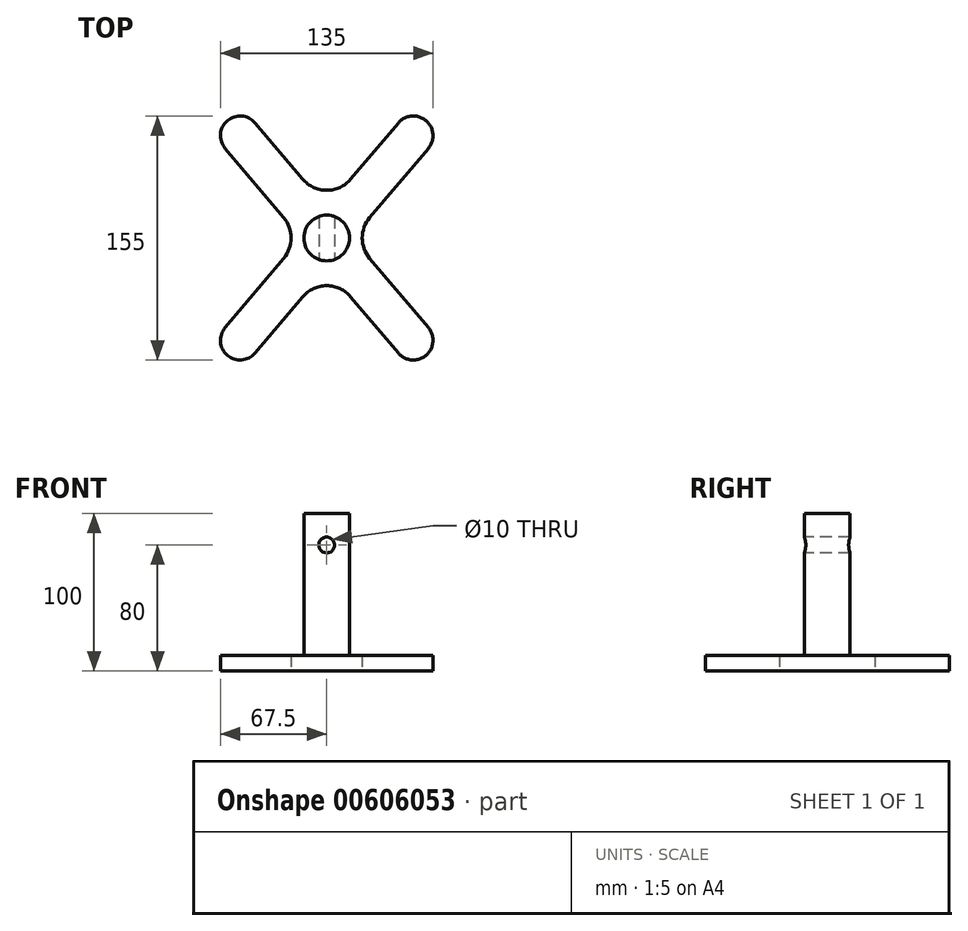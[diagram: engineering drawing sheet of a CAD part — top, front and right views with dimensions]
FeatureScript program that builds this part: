
annotation { "Feature Type Name" : "Feature", "Feature Type Description" : "" }
export const myFeature = defineFeature(function(context is Context, id is Id, definition is map)
    precondition{}
    {
        {
            var Q0;
            Q0=qCreatedBy(makeId("Top.planeOp"),FACE);
            var sketch = newSketch(context, id + "F0", { "sketchPlane" : qUnion([Q0])});
            skPoint(sketch, "E0.middle", {"position": v(0, 0) * mm});
            skLineSegment(sketch, "E1", {"start": v(-55, 65) * mm, "end": v(55, -65) * mm});
            skLineSegment(sketch, "E2", {"start": v(-55, -65) * mm, "end": v(55, 65) * mm});
            skCircle(sketch, "E3", {"center": v(-55, -65) * mm, "radius": 12.5 * mm});
            skCircle(sketch, "E4", {"center": v(-55, 65) * mm, "radius": 12.5 * mm});
            skCircle(sketch, "E5", {"center": v(55, 65) * mm, "radius": 12.5 * mm});
            skCircle(sketch, "E6", {"center": v(55, -65) * mm, "radius": 12.5 * mm});
            skLineSegment(sketch, "E7", {"start": v(-55, -65) * mm, "end": v(-64.54, -56.93) * mm});
            skLineSegment(sketch, "E8", {"start": v(-64.54, -56.93) * mm, "end": v(-45.46, -73.07) * mm});
            skLineSegment(sketch, "E9", {"start": v(-55, 65) * mm, "end": v(-64.54, 56.93) * mm});
            skLineSegment(sketch, "E10", {"start": v(-64.54, 56.93) * mm, "end": v(-45.46, 73.07) * mm});
            skLineSegment(sketch, "E11", {"start": v(55, 65) * mm, "end": v(45.46, 73.07) * mm});
            skLineSegment(sketch, "E12", {"start": v(45.46, 73.07) * mm, "end": v(64.54, 56.93) * mm});
            skLineSegment(sketch, "E13", {"start": v(55, -65) * mm, "end": v(45.46, -73.07) * mm});
            skLineSegment(sketch, "E14", {"start": v(45.46, -73.07) * mm, "end": v(64.54, -56.93) * mm});
            skLineSegment(sketch, "E15", {"start": v(-45.46, -73.07) * mm, "end": v(-15.27, -37.4) * mm});
            skLineSegment(sketch, "E16", {"start": v(-64.54, -56.93) * mm, "end": v(-27.3, -12.92) * mm});
            skLineSegment(sketch, "E17", {"start": v(-64.54, 56.93) * mm, "end": v(-27.3, 12.92) * mm});
            skLineSegment(sketch, "E18", {"start": v(64.54, -56.93) * mm, "end": v(27.3, -12.92) * mm});
            skArc(sketch, "E19.filletArc", {"start": v(-27.3, -12.92) * mm, "mid": v(-22.57, 0) * mm, "end": v(-27.3, 12.92) * mm});
            skLineSegment(sketch, "E20", {"start": v(45.46, -73.07) * mm, "end": v(15.27, -37.4) * mm});
            skArc(sketch, "E21.filletArc", {"start": v(15.27, -37.4) * mm, "mid": v(0, -30.31) * mm, "end": v(-15.27, -37.4) * mm});
            skLineSegment(sketch, "E22", {"start": v(45.46, 73.07) * mm, "end": v(15.27, 37.4) * mm});
            skLineSegment(sketch, "E23", {"start": v(64.54, 56.93) * mm, "end": v(27.3, 12.92) * mm});
            skArc(sketch, "E24.filletArc", {"start": v(27.3, 12.92) * mm, "mid": v(22.57, 0) * mm, "end": v(27.3, -12.92) * mm});
            skLineSegment(sketch, "E25", {"start": v(-45.46, 73.07) * mm, "end": v(-15.27, 37.4) * mm});
            skArc(sketch, "E26.filletArc", {"start": v(-15.27, 37.4) * mm, "mid": v(0, 30.31) * mm, "end": v(15.27, 37.4) * mm});
            skCircle(sketch, "E27", {"center": v(0, 0) * mm, "radius": 14.5 * mm});
            skSolve(sketch);
        }
        {
            var Q0;
            {var subQ0=sQuery(id+"F0.wireOp",EDGE,"E10");var subQ4=makeQuery(id+"F0.imprint","INTERSECT",VERTEX,{"derivedFrom":[sQuery(id+"F0.wireOp",EDGE,"E1"),subQ0]});Q0=makeQuery(id+"F0.imprint","IMPRINT",FACE,{"disambiguationData":[TD([[makeQuery(id+"F0.imprint","IMPRINT",EDGE,{"disambiguationData":[TD([[subQ4,1.0]])],"derivedFrom":subQ0}),1.0]])]});}
            var Q1;
            {var subQ0=sQuery(id+"F0.wireOp",EDGE,"E10");var subQ1=sQuery(id+"F0.wireOp",EDGE,"E1");var subQ2=makeQuery(id+"F0.imprint","INTERSECT",VERTEX,{"derivedFrom":[subQ1,subQ0]});Q1=makeQuery(id+"F0.imprint","IMPRINT",FACE,{"disambiguationData":[TD([[makeQuery(id+"F0.imprint","IMPRINT",EDGE,{"disambiguationData":[TD([[subQ2,-1.0]])],"derivedFrom":subQ1}),1.0]])]});}
            var Q2;
            {var subQ0=sQuery(id+"F0.wireOp",EDGE,"E10");var subQ1=sQuery(id+"F0.wireOp",EDGE,"E1");var subQ2=makeQuery(id+"F0.imprint","INTERSECT",VERTEX,{"derivedFrom":[subQ1,subQ0]});Q2=makeQuery(id+"F0.imprint","IMPRINT",FACE,{"disambiguationData":[TD([[makeQuery(id+"F0.imprint","IMPRINT",EDGE,{"disambiguationData":[TD([[subQ2,-1.0]])],"derivedFrom":subQ1}),-1.0]])]});}
            var Q3;
            {var subQ0=sQuery(id+"F0.wireOp",EDGE,"E22");Q3=makeQuery(id+"F0.imprint","IMPRINT",FACE,{"disambiguationData":[TD([[makeQuery(id+"F0.imprint","IMPRINT",EDGE,{"derivedFrom":subQ0}),1.0]])]});}
            var Q4;
            {var subQ10=sQuery(id+"F0.wireOp",EDGE,"E16");Q4=makeQuery(id+"F0.imprint","IMPRINT",FACE,{"disambiguationData":[TD([[makeQuery(id+"F0.imprint","IMPRINT",EDGE,{"derivedFrom":subQ10}),-1.0]])]});}
            var Q5;
            {var subQ0=sQuery(id+"F0.wireOp",EDGE,"E15");Q5=makeQuery(id+"F0.imprint","IMPRINT",FACE,{"disambiguationData":[TD([[makeQuery(id+"F0.imprint","IMPRINT",EDGE,{"derivedFrom":subQ0}),1.0]])]});}
            var Q6;
            {var subQ0=sQuery(id+"F0.wireOp",EDGE,"E18");Q6=makeQuery(id+"F0.imprint","IMPRINT",FACE,{"disambiguationData":[TD([[makeQuery(id+"F0.imprint","IMPRINT",EDGE,{"derivedFrom":subQ0}),1.0]])]});}
            var Q7;
            {var subQ0=sQuery(id+"F0.wireOp",EDGE,"E12");var subQ1=sQuery(id+"F0.wireOp",EDGE,"E2");var subQ2=makeQuery(id+"F0.imprint","INTERSECT",VERTEX,{"derivedFrom":[subQ1,subQ0]});Q7=makeQuery(id+"F0.imprint","IMPRINT",FACE,{"disambiguationData":[TD([[makeQuery(id+"F0.imprint","IMPRINT",EDGE,{"disambiguationData":[TD([[subQ2,1.0]])],"derivedFrom":subQ1}),-1.0]])]});}
            var Q8;
            {var subQ0=sQuery(id+"F0.wireOp",EDGE,"E12");var subQ1=sQuery(id+"F0.wireOp",EDGE,"E2");var subQ2=makeQuery(id+"F0.imprint","INTERSECT",VERTEX,{"derivedFrom":[subQ1,subQ0]});Q8=makeQuery(id+"F0.imprint","IMPRINT",FACE,{"disambiguationData":[TD([[makeQuery(id+"F0.imprint","IMPRINT",EDGE,{"disambiguationData":[TD([[subQ2,1.0]])],"derivedFrom":subQ1}),1.0]])]});}
            var Q9;
            {var subQ0=sQuery(id+"F0.wireOp",EDGE,"E12");var subQ4=makeQuery(id+"F0.imprint","INTERSECT",VERTEX,{"derivedFrom":[sQuery(id+"F0.wireOp",EDGE,"E2"),subQ0]});Q9=makeQuery(id+"F0.imprint","IMPRINT",FACE,{"disambiguationData":[TD([[makeQuery(id+"F0.imprint","IMPRINT",EDGE,{"disambiguationData":[TD([[subQ4,1.0]])],"derivedFrom":subQ0}),1.0]])]});}
            var Q10;
            {var subQ0=sQuery(id+"F0.wireOp",EDGE,"E8");var subQ1=sQuery(id+"F0.wireOp",EDGE,"E2");var subQ2=makeQuery(id+"F0.imprint","INTERSECT",VERTEX,{"derivedFrom":[subQ1,subQ0]});Q10=makeQuery(id+"F0.imprint","IMPRINT",FACE,{"disambiguationData":[TD([[makeQuery(id+"F0.imprint","IMPRINT",EDGE,{"disambiguationData":[TD([[subQ2,-1.0]])],"derivedFrom":subQ1}),-1.0]])]});}
            var Q11;
            {var subQ0=sQuery(id+"F0.wireOp",EDGE,"E8");var subQ1=sQuery(id+"F0.wireOp",EDGE,"E2");var subQ2=makeQuery(id+"F0.imprint","INTERSECT",VERTEX,{"derivedFrom":[subQ1,subQ0]});Q11=makeQuery(id+"F0.imprint","IMPRINT",FACE,{"disambiguationData":[TD([[makeQuery(id+"F0.imprint","IMPRINT",EDGE,{"disambiguationData":[TD([[subQ2,-1.0]])],"derivedFrom":subQ1}),1.0]])]});}
            var Q12;
            {var subQ0=sQuery(id+"F0.wireOp",EDGE,"E8");var subQ4=makeQuery(id+"F0.imprint","INTERSECT",VERTEX,{"derivedFrom":[sQuery(id+"F0.wireOp",EDGE,"E2"),subQ0]});Q12=makeQuery(id+"F0.imprint","IMPRINT",FACE,{"disambiguationData":[TD([[makeQuery(id+"F0.imprint","IMPRINT",EDGE,{"disambiguationData":[TD([[subQ4,1.0]])],"derivedFrom":subQ0}),-1.0]])]});}
            var Q13;
            {var subQ0=sQuery(id+"F0.wireOp",EDGE,"E14");var subQ4=makeQuery(id+"F0.imprint","INTERSECT",VERTEX,{"derivedFrom":[sQuery(id+"F0.wireOp",EDGE,"E1"),subQ0]});Q13=makeQuery(id+"F0.imprint","IMPRINT",FACE,{"disambiguationData":[TD([[makeQuery(id+"F0.imprint","IMPRINT",EDGE,{"disambiguationData":[TD([[subQ4,1.0]])],"derivedFrom":subQ0}),-1.0]])]});}
            var Q14;
            {var subQ0=sQuery(id+"F0.wireOp",EDGE,"E14");var subQ1=sQuery(id+"F0.wireOp",EDGE,"E1");var subQ2=makeQuery(id+"F0.imprint","INTERSECT",VERTEX,{"derivedFrom":[subQ1,subQ0]});Q14=makeQuery(id+"F0.imprint","IMPRINT",FACE,{"disambiguationData":[TD([[makeQuery(id+"F0.imprint","IMPRINT",EDGE,{"disambiguationData":[TD([[subQ2,1.0]])],"derivedFrom":subQ1}),-1.0]])]});}
            var Q15;
            {var subQ0=sQuery(id+"F0.wireOp",EDGE,"E14");var subQ1=sQuery(id+"F0.wireOp",EDGE,"E1");var subQ2=makeQuery(id+"F0.imprint","INTERSECT",VERTEX,{"derivedFrom":[subQ1,subQ0]});Q15=makeQuery(id+"F0.imprint","IMPRINT",FACE,{"disambiguationData":[TD([[makeQuery(id+"F0.imprint","IMPRINT",EDGE,{"disambiguationData":[TD([[subQ2,1.0]])],"derivedFrom":subQ1}),1.0]])]});}
            var Q16;
            {var subQ0=sQuery(id+"F0.wireOp",EDGE,"saydBoC8-mGO9-YOxe-JXCX-vK9WEqxBoyUe");var subQ1=sQuery(id+"F0.wireOp",EDGE,"E1");var subQ2=makeQuery(id+"F0.imprint","INTERSECT",VERTEX,{"disambiguationData":[OD(0.0)],"derivedFrom":[subQ1,subQ0]});Q16=makeQuery(id+"F0.imprint","IMPRINT",FACE,{"disambiguationData":[TD([[makeQuery(id+"F0.imprint","IMPRINT",EDGE,{"disambiguationData":[TD([[subQ2,-1.0]])],"derivedFrom":subQ1}),1.0]])]});}
            var Q17;
            {var subQ0=sQuery(id+"F0.wireOp",EDGE,"saydBoC8-mGO9-YOxe-JXCX-vK9WEqxBoyUe");var subQ1=sQuery(id+"F0.wireOp",EDGE,"E1");var subQ2=makeQuery(id+"F0.imprint","INTERSECT",VERTEX,{"disambiguationData":[OD(0.0)],"derivedFrom":[subQ1,subQ0]});Q17=makeQuery(id+"F0.imprint","IMPRINT",FACE,{"disambiguationData":[TD([[makeQuery(id+"F0.imprint","IMPRINT",EDGE,{"disambiguationData":[TD([[subQ2,-1.0]])],"derivedFrom":subQ1}),-1.0]])]});}
            var Q18;
            {var subQ0=sQuery(id+"F0.wireOp",EDGE,"E2");var subQ1=sQuery(id+"F0.wireOp",EDGE,"E1");var subQ2=makeQuery(id+"F0.imprint","INTERSECT",VERTEX,{"derivedFrom":[subQ1,subQ0]});Q18=makeQuery(id+"F0.imprint","IMPRINT",FACE,{"disambiguationData":[TD([[makeQuery(id+"F0.imprint","IMPRINT",EDGE,{"disambiguationData":[TD([[subQ2,-1.0]])],"derivedFrom":subQ1}),1.0]])]});}
            var Q19;
            {var subQ0=sQuery(id+"F0.wireOp",EDGE,"E2");var subQ1=sQuery(id+"F0.wireOp",EDGE,"E1");var subQ2=makeQuery(id+"F0.imprint","INTERSECT",VERTEX,{"derivedFrom":[subQ1,subQ0]});Q19=makeQuery(id+"F0.imprint","IMPRINT",FACE,{"disambiguationData":[TD([[makeQuery(id+"F0.imprint","IMPRINT",EDGE,{"disambiguationData":[TD([[subQ2,-1.0]])],"derivedFrom":subQ1}),-1.0]])]});}
            var Q20;
            {var subQ0=sQuery(id+"F0.wireOp",EDGE,"E27");var subQ1=sQuery(id+"F0.wireOp",EDGE,"E1");var subQ2=makeQuery(id+"F0.imprint","INTERSECT",VERTEX,{"disambiguationData":[OD(0.0)],"derivedFrom":[subQ1,subQ0]});Q20=makeQuery(id+"F0.imprint","IMPRINT",FACE,{"disambiguationData":[TD([[makeQuery(id+"F0.imprint","IMPRINT",EDGE,{"disambiguationData":[TD([[subQ2,-1.0]])],"derivedFrom":subQ1}),-1.0]])]});}
            var Q21;
            {var subQ0=sQuery(id+"F0.wireOp",EDGE,"E27");var subQ1=sQuery(id+"F0.wireOp",EDGE,"E1");var subQ2=makeQuery(id+"F0.imprint","INTERSECT",VERTEX,{"disambiguationData":[OD(0.0)],"derivedFrom":[subQ1,subQ0]});Q21=makeQuery(id+"F0.imprint","IMPRINT",FACE,{"disambiguationData":[TD([[makeQuery(id+"F0.imprint","IMPRINT",EDGE,{"disambiguationData":[TD([[subQ2,-1.0]])],"derivedFrom":subQ1}),1.0]])]});}
            extrude(context, id + "F1", {"entities" : qUnion([Q0, Q1, Q2, Q3, Q4, Q5, Q6, Q7, Q8, Q9, Q10, Q11, Q12, Q13, Q14, Q15, Q16, Q17, Q18, Q19, Q20, Q21]), "depth" : 10 * mm, "offsetDistance" : 25 * mm});
        }
        {
            var Q0;
            Q0=qCreatedBy(makeId("Front.planeOp"),FACE);
            var sketch = newSketch(context, id + "F2", { "sketchPlane" : qUnion([Q0])});
            skCircle(sketch, "E28", {"center": v(0, 80) * mm, "radius": 5 * mm});
            skSolve(sketch);
        }
        {
            var Q0;
            Q0=makeQuery(id+"F1.opExtrude","CAP_FACE",FACE,{"disambiguationData":[OSD([sQuery(id+"F0.wireOp",EDGE,"E3"),sQuery(id+"F0.wireOp",EDGE,"E4"),sQuery(id+"F0.wireOp",EDGE,"E5"),sQuery(id+"F0.wireOp",EDGE,"E6"),sQuery(id+"F0.wireOp",EDGE,"E15"),sQuery(id+"F0.wireOp",EDGE,"E16"),sQuery(id+"F0.wireOp",EDGE,"E17"),sQuery(id+"F0.wireOp",EDGE,"E18"),sQuery(id+"F0.wireOp",EDGE,"E19.filletArc"),sQuery(id+"F0.wireOp",EDGE,"E20"),sQuery(id+"F0.wireOp",EDGE,"E21.filletArc"),sQuery(id+"F0.wireOp",EDGE,"E22"),sQuery(id+"F0.wireOp",EDGE,"E23"),sQuery(id+"F0.wireOp",EDGE,"E24.filletArc"),sQuery(id+"F0.wireOp",EDGE,"E25"),sQuery(id+"F0.wireOp",EDGE,"E26.filletArc")])],"isStart":false});
            var sketch = newSketch(context, id + "F3", { "sketchPlane" : qUnion([Q0])});
            skCircle(sketch, "E29", {"center": v(0, 0) * mm, "radius": 14.5 * mm});
            skSolve(sketch);
        }
        {
            var Q0;
            Q0=makeQuery(id+"F3.imprint","IMPRINT",FACE,{"disambiguationData":[TD([[makeQuery(id+"F3.imprint","IMPRINT",EDGE,{"derivedFrom":sQuery(id+"F3.wireOp",EDGE,"E29")}),1.0]])]});
            extrude(context, id + "F4", {"entities" : qUnion([Q0]), "operationType" : NewBodyOperationType.ADD, "depth" : 90 * mm, "offsetDistance" : 25 * mm});
        }
        {
            var Q0;
            Q0 = qSketchRegion(id + "F2", true);
            extrude(context, id + "F5", {"entities" : qUnion([Q0]), "operationType" : NewBodyOperationType.REMOVE, "endBound" : BoundingType.SYMMETRIC, "oppositeDirection" : true, "depth" : 50 * mm, "offsetDistance" : 25 * mm});
        }
    });
